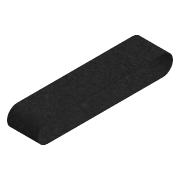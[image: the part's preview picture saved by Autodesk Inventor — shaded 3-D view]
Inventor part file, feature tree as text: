
AUTODESK INVENTOR PART (.ipt)
format: ipt  version: 2022 (Build 260153000, 153)  size: 134,656 bytes
history: native  units: mm
features: extrude x2, sketch x2, fillet x1, projected_geometry x1
ambient origin geometry x8: Origin, YZ Plane, XZ Plane, XY Plane, X Axis, Y Axis, Z Axis, Center Point
bodies: Body1 (feature_tree)
feature tree (6):
  extrude  "Выдавливание2"  Depth=200.0mm
  fillet  "Сопряжение1"  Radius=30.0mm
  extrude  "Выдавливание3"  Depth=45.0mm TaperAngle=0.0deg
  sketch  "Эскиз1"
  sketch  "Эскиз2"
  projected_geometry  "Спроецированная петля1"
